# Revit family: TD92_PUF426_BRA010_RVT20_R00
name_source: partatom
category: Mobiliário
units: mm (PartAtom-declared; Revit-internal decimal feet)

## family parameters
Com base no plano de trabalho = Não
Compartilhado = Não
Corte com vazios quando carregada = Não
Número OmniClass = 23.40.20.00
Ponto de cálculo do ambiente = Não
Sempre na vertical = Sim
Título OmniClass = General Furniture and Specialties

## types (1)
- TD92_PUF426_BRA010_RVT20_R00
    Descrição = O Puff Multiuso Tramontina em Polipropileno atende as necessidades que você encontrar no dia a dia. Com design diferenciado e cheio de estilo, ele é uma peça funcional que serve desde guarda trecos até vaso, por isso, é perfeito para qualquer ambiente. Produzido em polipropileno, é uma peça única que atende as tarefas que você desejar. O produto perfeito para sua casa!
    Elevação padrão = 0  [stored 0 ft]
    Fabricante = Tramontina Delta S/A
    Modelo = Puff Multiuso Tramontina em Polipropileno Branco
    Nota-chave = 92426010
    URL = https://www.tramontinastore.com

note: [stored X ft] marks values corroborated as IEEE doubles in the binary element streams (Revit-internal decimal feet)
